# Revit family: Varmax 120-140_4 tomas
name_source: partatom
category: Mechanical Equipment
revit_build: Autodesk Revit 2014 (Build: 20130308_1515(x64)
units: mm (PartAtom-declared; Revit-internal decimal feet)

## types (2) — shared parameters
Alt. conec. = 1256 mm
Alt. derivacion gas = 1062 mm
Alt. entrada de aire = 1298 mm
Alt. entrada/salida retorno = 926 mm
Altura = 1530 mm
Ancho = 734 mm  [stored 2.40814 ft]
Assembly Code = D3020100
Caudal de gas a Pn (15 ºC) = 12,7 m3/h
Conector = 148 mm
Configuración = 4 tomas
Derivación de gas = 32 mm
Derivación de vaciado = 25 mm  [stored 0.082021 ft]
Derivación salida / retorno = 51 mm
Empresa creadora del BIM = ACAE
Entrada de aire = 150 mm
Manufacturer = Atlantic
Mínimo = 45 mm
Peso en vacío = 420 kg
Presión máxima de servicio = 6 bar
Profundidad Total = 1189 mm
Rendimiento mínimo al 100% de potencia (80/60 ºC) = 97,7%
Rendimiento mínimo al 30% de carga (50/30 ºC) = 108,8%
Salida de humo = 150 mm
Salida de humos = 150 mm
Tipo de combustible = Gas natural (G20), en opción Gas propano (G31) hasta 320 kW.
URL = http://www.ygnis.es
Volumen de agua = 116 L

## per-type parameters (varying)
| type | Consumo eléctrico máximo | Description | Model | Potencia útil a (50/30 ºC) |
| Varmax 120 - Caldera de pie de condensación a gas 127 kW y 6 bar (4 tomas) | 204 W | Unidad térmica de condensación para gas natural Ygnis modelo Varmax 120,  potencia útil (50/30 ºC) de 127 kW. Fabricada en acero inoxidable de alta calidad AISI 316 L. Quemador modulante desde el 20% de la potencia. Rendimiento hasta el 107.4 %. Clase 5 de NOx. Dimensiones (Altura x Ancho x Largo): 1584 x 700 x 1172 mm. Peso en vacío: 420 kg. Presión máxima de servicio: 6 bar. Configuración a 4 tomas. | Varmax 120 | 127 kW |
| Varmax 140 - Caldera de pie de condensación a gas 148 kW y 6 bar (4 tomas) | 311 W | Unidad térmica de condensación para gas natural Ygnis modelo Varmax 140,  potencia útil (50/30 ºC) de 148 kW. Fabricada en acero inoxidable de alta calidad AISI 316 L. Quemador modulante desde el 20% de la potencia. Rendimiento hasta el 107.4 %. Clase 5 de NOx. Dimensiones (Altura x Ancho x Largo): 1584 x 700 x 1172 mm. Peso en vacío: 420 kg. Presión máxima de servicio: 6 bar. Configuración a 4 tomas. | Varmax 140 | 148 kW |

note: [stored X ft] marks values corroborated as IEEE doubles in the binary element streams (Revit-internal decimal feet)

## geometry (parser evidence)
native form markers: Sweep x2
no freeform markers — native parametric forms only
